# Revit family: 351_38310
name_source: partatom
category: Plumbing Fixtures
units: mm (PartAtom-declared; Revit-internal decimal feet)

## family parameters
Always vertical = Yes
Cut with Voids When Loaded = No
Part Type = Normal
Room Calculation Point = No
Round Connector Dimension = Use Diameter
Shared = No
Work Plane-Based = No

## types (1)
- 5650119 IDO Seven D
    CARM = No
    CAT0 = Yes
    CLBTZ = 0 mm  [stored 0 ft]
    CL_Location_5000 = 5000 mm
    DC = 110 mm
    Description = WC SEVEN D, concealed outlet without fastening holes in the foot, soft seat
    MC Product Code = 5650119 IDO Seven D
    Manufacturer = IDO
    QmdConnectorList = 601;DC
    URL = http://www.ido.fi
    magiPartTypeId = 351
    magiProductFamilyId = 38310
    magiProductId = 38310

note: [stored X ft] marks values corroborated as IEEE doubles in the binary element streams (Revit-internal decimal feet)

## geometry (parser evidence)
native form markers: Sweep x2
no freeform markers — native parametric forms only
